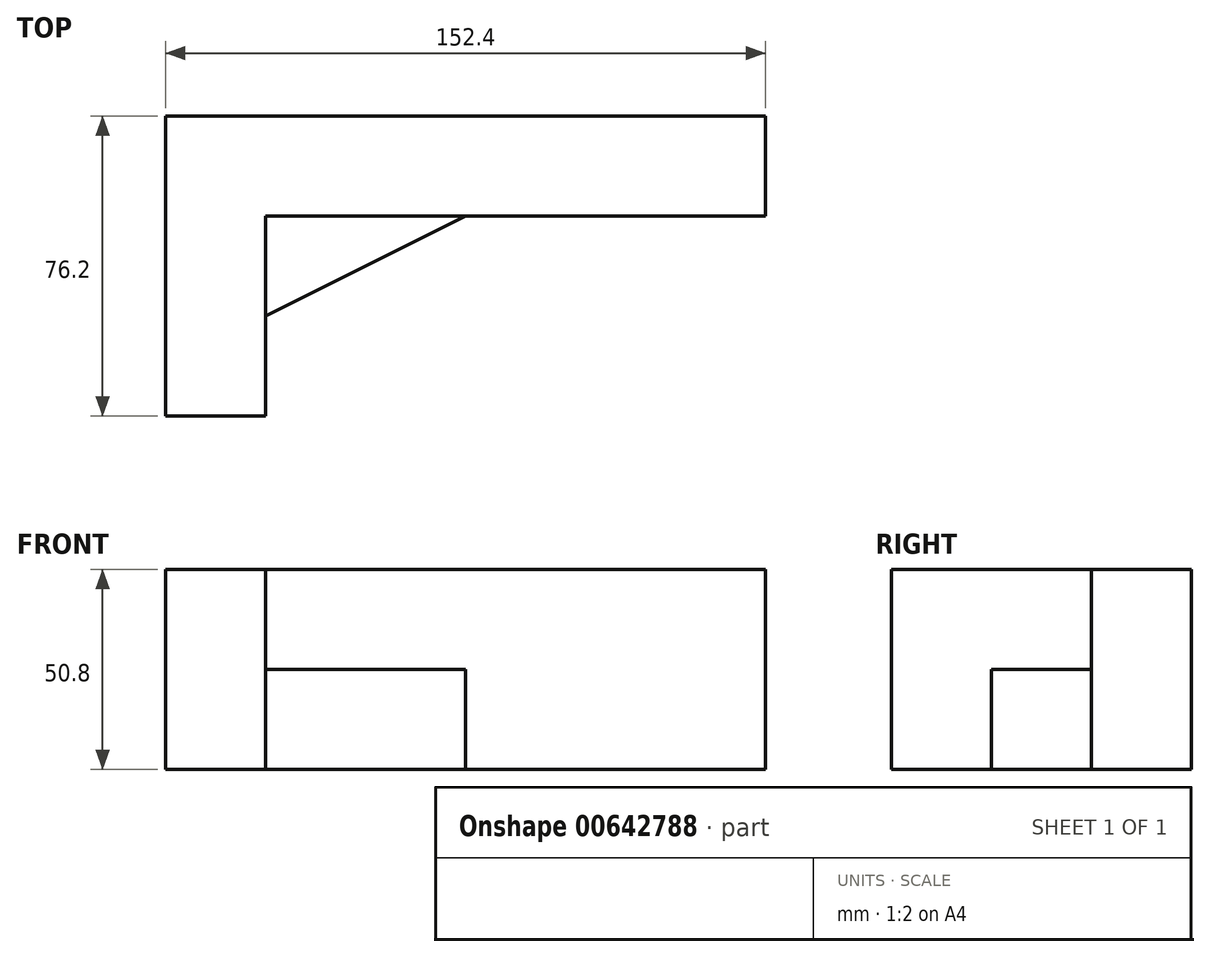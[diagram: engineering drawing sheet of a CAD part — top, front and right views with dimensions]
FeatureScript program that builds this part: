
annotation { "Feature Type Name" : "Feature", "Feature Type Description" : "" }
export const myFeature = defineFeature(function(context is Context, id is Id, definition is map)
    precondition{}
    {
        {
            var Q0;
            Q0=qCreatedBy(makeId("Front.planeOp"),FACE);
            var sketch = newSketch(context, id + "F0", { "sketchPlane" : qUnion([Q0])});
            skLineSegment(sketch, "E0", {"start": v(0, 0) * mm, "end": v(-152.4, 0) * mm});
            skLineSegment(sketch, "E1", {"start": v(-152.4, 0) * mm, "end": v(-152.4, 50.8) * mm});
            skLineSegment(sketch, "E2", {"start": v(-152.4, 50.8) * mm, "end": v(0, 50.8) * mm});
            skLineSegment(sketch, "E3", {"start": v(0, 50.8) * mm, "end": v(0, 0) * mm});
            skSolve(sketch);
        }
        {
            var Q0;
            Q0 = qSketchRegion(id + "F0", true);
            extrude(context, id + "F1", {"entities" : qUnion([Q0]), "depth" : 76.2 * mm, "offsetDistance" : 25.4 * mm});
        }
        {
            var Q0;
            Q0=makeQuery(id+"F1.opExtrude","SWEPT_FACE",FACE,{"disambiguationData":[OSD([sQuery(id+"F0.wireOp",EDGE,"E3")])]});
            var sketch = newSketch(context, id + "F2", { "sketchPlane" : qUnion([Q0])});
            skLineSegment(sketch, "E4", {"start": v(-76.2, 50.8) * mm, "end": v(-76.2, 25.4) * mm});
            skLineSegment(sketch, "E5", {"start": v(-76.2, 25.4) * mm, "end": v(-25.4, 25.4) * mm});
            skLineSegment(sketch, "E6", {"start": v(-25.4, 25.4) * mm, "end": v(-25.4, 50.8) * mm});
            skLineSegment(sketch, "E7", {"start": v(-25.4, 50.8) * mm, "end": v(-76.2, 50.8) * mm});
            skSolve(sketch);
        }
        {
            var Q0;
            Q0 = qSketchRegion(id + "F2", true);
            extrude(context, id + "F3", {"entities" : qUnion([Q0]), "operationType" : NewBodyOperationType.REMOVE, "oppositeDirection" : true, "depth" : 127 * mm, "offsetDistance" : 25.4 * mm});
        }
        {
            var Q0;
            Q0=makeQuery(id+"F3.boolean.opBoolean","COPY",FACE,{"derivedFrom":makeQuery(id+"F3.opExtrude","SWEPT_FACE",FACE,{"disambiguationData":[OSD([sQuery(id+"F2.wireOp",EDGE,"E5")])]})});
            var sketch = newSketch(context, id + "F4", { "sketchPlane" : qUnion([Q0])});
            skLineSegment(sketch, "E8", {"start": v(-127, -25.4) * mm, "end": v(-127, -50.8) * mm});
            skLineSegment(sketch, "E9", {"start": v(-127, -50.8) * mm, "end": v(-76.2, -25.4) * mm});
            skLineSegment(sketch, "E10", {"start": v(-76.2, -25.4) * mm, "end": v(-127, -25.4) * mm});
            skLineSegment(sketch, "E11", {"start": v(-127, -50.8) * mm, "end": v(-127, -25.4) * mm});
            skSolve(sketch);
        }
        {
            var Q0;
            {var subQ3=sQuery(id+"F4.wireOp",EDGE,"E9");Q0=makeQuery(id+"F4.imprint","IMPRINT",FACE,{"disambiguationData":[TD([[makeQuery(id+"F4.imprint","IMPRINT",EDGE,{"derivedFrom":subQ3}),-1.0]])]});}
            var sketch = newSketch(context, id + "F5", { "sketchPlane" : qUnion([Q0])});
            skSolve(sketch);
        }
        {
            var Q0;
            Q0 = qSketchRegion(id + "F5", true);
            var Q1;
            {var subQ3=sQuery(id+"F4.wireOp",EDGE,"E9");Q1=makeQuery(id+"F4.imprint","IMPRINT",FACE,{"disambiguationData":[TD([[makeQuery(id+"F4.imprint","IMPRINT",EDGE,{"derivedFrom":subQ3}),-1.0]])]});}
            extrude(context, id + "F6", {"entities" : qUnion([Q0, Q1]), "operationType" : NewBodyOperationType.REMOVE, "oppositeDirection" : true, "depth" : 25.4 * mm, "offsetDistance" : 25.4 * mm});
        }
    });
